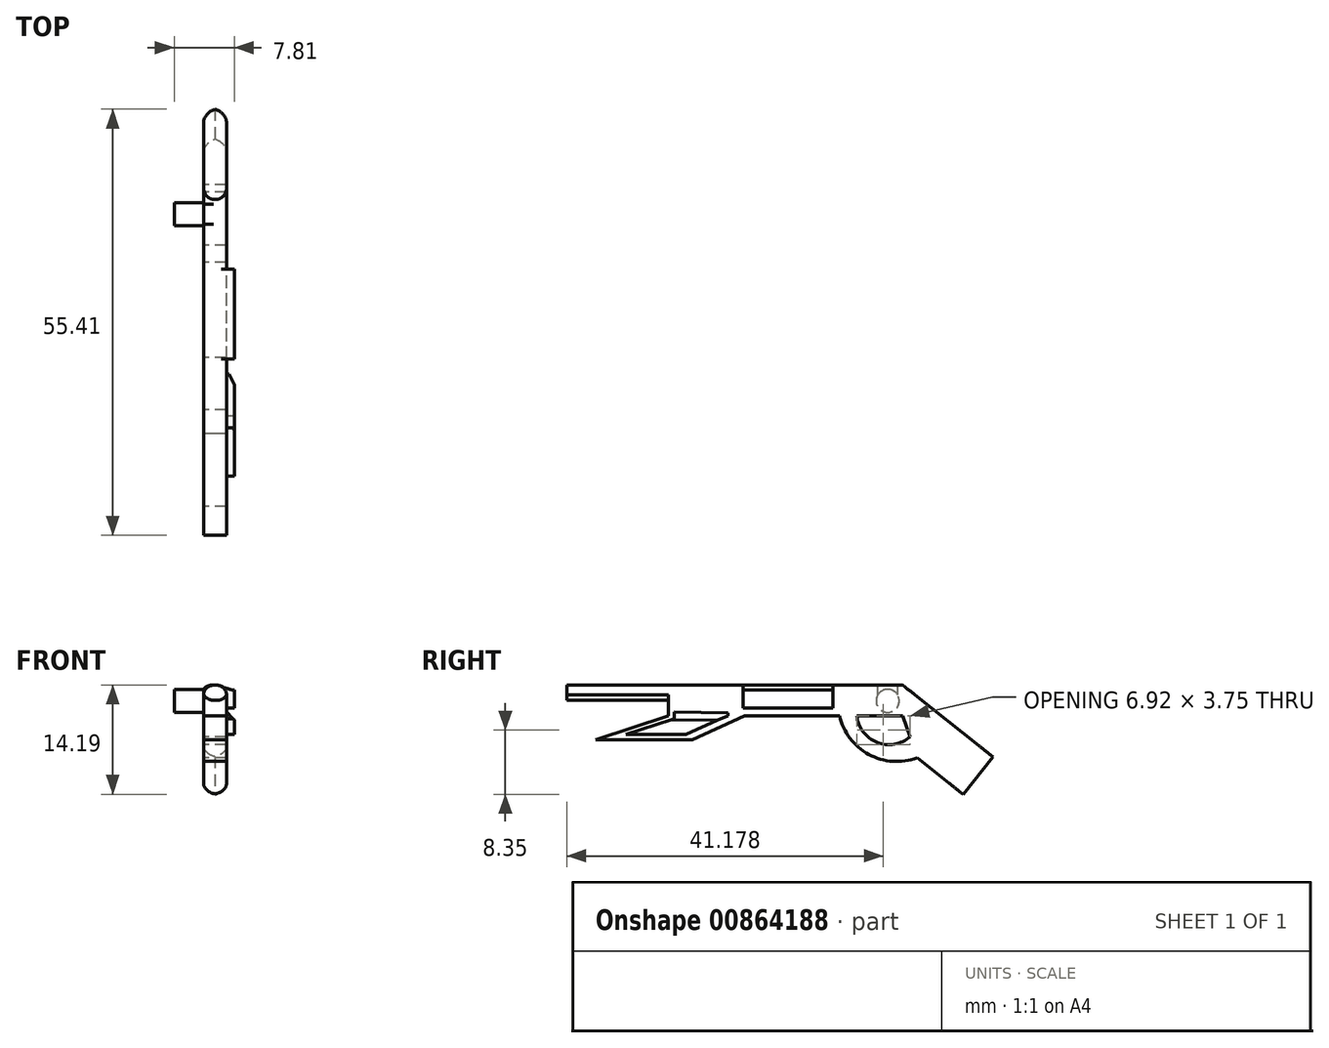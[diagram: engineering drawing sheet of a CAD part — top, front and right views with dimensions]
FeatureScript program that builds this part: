
annotation { "Feature Type Name" : "Feature", "Feature Type Description" : "" }
export const myFeature = defineFeature(function(context is Context, id is Id, definition is map)
    precondition{}
    {
        {
            var Q0;
            Q0=qCreatedBy(makeId("Right.planeOp"),FACE);
            var sketch = newSketch(context, id + "F0", { "sketchPlane" : qUnion([Q0])});
            skLineSegment(sketch, "E0.bottom", {"start": v(-13.26, 14.33) * mm, "end": v(17.22, 14.33) * mm});
            skLineSegment(sketch, "E0.top", {"start": v(-13.26, 10.36) * mm, "end": v(17.22, 10.36) * mm});
            skLineSegment(sketch, "E0.left", {"start": v(-13.26, 14.33) * mm, "end": v(-13.26, 10.36) * mm});
            skLineSegment(sketch, "E0.right", {"start": v(17.22, 14.33) * mm, "end": v(17.22, 10.36) * mm});
            skLineSegment(sketch, "E1", {"start": v(17.22, 14.33) * mm, "end": v(29.1, 4.88) * mm});
            skLineSegment(sketch, "E2", {"start": v(29.1, 4.88) * mm, "end": v(25.23, 0) * mm});
            skLineSegment(sketch, "E3", {"start": v(25.23, 0) * mm, "end": v(19.1, 4.88) * mm});
            skLineSegment(sketch, "E4", {"start": v(19.1, 4.88) * mm, "end": v(17.22, 10.36) * mm});
            skArc(sketch, "E5", {"start": v(9, 10.36) * mm, "mid": v(12.8, 5.32) * mm, "end": v(19.1, 4.88) * mm});
            skArc(sketch, "E6", {"start": v(11.24, 10.36) * mm, "mid": v(13.86, 6.89) * mm, "end": v(18.16, 7.62) * mm});
            skLineSegment(sketch, "E7", {"start": v(-3.39, 10.36) * mm, "end": v(-10.19, 7.24) * mm});
            skLineSegment(sketch, "E8", {"start": v(-10.19, 7.24) * mm, "end": v(-22.76, 7.24) * mm});
            skLineSegment(sketch, "E9", {"start": v(-22.76, 7.24) * mm, "end": v(-13.26, 10.36) * mm});
            skLineSegment(sketch, "E10", {"start": v(-13.26, 12.34) * mm, "end": v(-26.48, 12.34) * mm});
            skLineSegment(sketch, "E11", {"start": v(-26.48, 12.34) * mm, "end": v(-26.48, 14.33) * mm});
            skLineSegment(sketch, "E12", {"start": v(-26.48, 14.33) * mm, "end": v(-13.26, 14.33) * mm});
            skSolve(sketch);
        }
        {
            var Q0;
            {var subQ2=sQuery(id+"F0.wireOp",EDGE,"E10");Q0=makeQuery(id+"F0.imprint","IMPRINT",FACE,{"disambiguationData":[TD([[makeQuery(id+"F0.imprint","IMPRINT",EDGE,{"derivedFrom":subQ2}),-1.0]])]});}
            var Q1;
            {var subQ2=sQuery(id+"F0.wireOp",EDGE,"E7");Q1=makeQuery(id+"F0.imprint","IMPRINT",FACE,{"disambiguationData":[TD([[makeQuery(id+"F0.imprint","IMPRINT",EDGE,{"derivedFrom":subQ2}),-1.0]])]});}
            var Q2;
            {var subQ6=sQuery(id+"F0.wireOp",EDGE,"E0.bottom");Q2=makeQuery(id+"F0.imprint","IMPRINT",FACE,{"disambiguationData":[TD([[makeQuery(id+"F0.imprint","IMPRINT",EDGE,{"derivedFrom":subQ6}),-1.0]])]});}
            var Q3;
            {var subQ0=sQuery(id+"F0.wireOp",EDGE,"E5");Q3=makeQuery(id+"F0.imprint","IMPRINT",FACE,{"disambiguationData":[TD([[makeQuery(id+"F0.imprint","IMPRINT",EDGE,{"derivedFrom":subQ0}),1.0]])]});}
            var Q4;
            {var subQ1=sQuery(id+"F0.wireOp",EDGE,"E0.right");Q4=makeQuery(id+"F0.imprint","IMPRINT",FACE,{"disambiguationData":[TD([[makeQuery(id+"F0.imprint","IMPRINT",EDGE,{"derivedFrom":subQ1}),1.0]])]});}
            extrude(context, id + "F1", {"entities" : qUnion([Q0, Q1, Q2, Q3, Q4]), "depth" : 3 * mm, "offsetDistance" : 25.4 * mm});
        }
        {
            var Q0;
            Q0=makeQuery(id+"F1.opExtrude","CAP_FACE",FACE,{"disambiguationData":[OSD([sQuery(id+"F0.wireOp",EDGE,"E0.bottom"),sQuery(id+"F0.wireOp",EDGE,"E0.top"),sQuery(id+"F0.wireOp",EDGE,"E0.left"),sQuery(id+"F0.wireOp",EDGE,"E1"),sQuery(id+"F0.wireOp",EDGE,"E2"),sQuery(id+"F0.wireOp",EDGE,"E3"),sQuery(id+"F0.wireOp",EDGE,"E4"),sQuery(id+"F0.wireOp",EDGE,"E5"),sQuery(id+"F0.wireOp",EDGE,"E6"),sQuery(id+"F0.wireOp",EDGE,"E7"),sQuery(id+"F0.wireOp",EDGE,"E8"),sQuery(id+"F0.wireOp",EDGE,"E9"),sQuery(id+"F0.wireOp",EDGE,"E10"),sQuery(id+"F0.wireOp",EDGE,"E11"),sQuery(id+"F0.wireOp",EDGE,"E12")])],"isStart":false});
            var sketch = newSketch(context, id + "F2", { "sketchPlane" : qUnion([Q0])});
            skLineSegment(sketch, "E13", {"start": v(-12.48, 12.39) * mm, "end": v(-12.48, 9.99) * mm});
            skLineSegment(sketch, "E14", {"start": v(-12.48, 9.99) * mm, "end": v(-18.8, 7.9) * mm});
            skLineSegment(sketch, "E15", {"start": v(-18.8, 7.9) * mm, "end": v(-10.97, 7.9) * mm});
            skLineSegment(sketch, "E16", {"start": v(-10.97, 7.9) * mm, "end": v(-5.54, 10.36) * mm});
            skLineSegment(sketch, "E17", {"start": v(-5.54, 10.36) * mm, "end": v(-5.54, 12.25) * mm});
            skLineSegment(sketch, "E18", {"start": v(-5.54, 12.25) * mm, "end": v(-12.48, 12.39) * mm});
            skLineSegment(sketch, "E19.bottom", {"start": v(-3.54, 13.68) * mm, "end": v(8.16, 13.68) * mm});
            skLineSegment(sketch, "E19.top", {"start": v(-3.54, 11.32) * mm, "end": v(8.16, 11.32) * mm});
            skLineSegment(sketch, "E19.left", {"start": v(-3.54, 13.68) * mm, "end": v(-3.54, 11.32) * mm});
            skLineSegment(sketch, "E19.right", {"start": v(8.16, 13.68) * mm, "end": v(8.16, 11.32) * mm});
            skSolve(sketch);
        }
        {
            var Q0;
            Q0=makeQuery(id+"F2.imprint","IMPRINT",FACE,{"disambiguationData":[TD([[makeQuery(id+"F2.imprint","IMPRINT",EDGE,{"derivedFrom":sQuery(id+"F2.wireOp",EDGE,"E13")}),1.0]])]});
            var Q1;
            Q1=makeQuery(id+"F2.imprint","IMPRINT",FACE,{"disambiguationData":[TD([[makeQuery(id+"F2.imprint","IMPRINT",EDGE,{"derivedFrom":sQuery(id+"F2.wireOp",EDGE,"E19.bottom")}),-1.0]])]});
            extrude(context, id + "F3", {"entities" : qUnion([Q0, Q1]), "operationType" : NewBodyOperationType.ADD, "depth" : 1 * mm, "offsetDistance" : 25.4 * mm});
        }
        {
            var Q0;
            Q0=makeQuery(id+"F1.opExtrude","CAP_FACE",FACE,{"disambiguationData":[OSD([sQuery(id+"F0.wireOp",EDGE,"E0.bottom"),sQuery(id+"F0.wireOp",EDGE,"E0.top"),sQuery(id+"F0.wireOp",EDGE,"E0.left"),sQuery(id+"F0.wireOp",EDGE,"E1"),sQuery(id+"F0.wireOp",EDGE,"E2"),sQuery(id+"F0.wireOp",EDGE,"E3"),sQuery(id+"F0.wireOp",EDGE,"E4"),sQuery(id+"F0.wireOp",EDGE,"E5"),sQuery(id+"F0.wireOp",EDGE,"E6"),sQuery(id+"F0.wireOp",EDGE,"E7"),sQuery(id+"F0.wireOp",EDGE,"E8"),sQuery(id+"F0.wireOp",EDGE,"E9"),sQuery(id+"F0.wireOp",EDGE,"E10"),sQuery(id+"F0.wireOp",EDGE,"E11"),sQuery(id+"F0.wireOp",EDGE,"E12")])],"isStart":true});
            var sketch = newSketch(context, id + "F4", { "sketchPlane" : qUnion([Q0])});
            skCircle(sketch, "E20", {"center": v(-15.26, 12.28) * mm, "radius": 1.5 * mm});
            skSolve(sketch);
        }
        {
            var Q0;
            Q0=makeQuery(id+"F4.imprint","IMPRINT",FACE,{"disambiguationData":[TD([[makeQuery(id+"F4.imprint","IMPRINT",EDGE,{"derivedFrom":sQuery(id+"F4.wireOp",EDGE,"E20")}),1.0]])]});
            extrude(context, id + "F5", {"entities" : qUnion([Q0]), "operationType" : NewBodyOperationType.ADD, "depth" : 3.8 * mm, "offsetDistance" : 25.4 * mm});
        }
        {
            var Q0;
            Q0=makeQuery(id+"F1.opExtrude","CAP_EDGE",EDGE,{"disambiguationData":[OSD([sQuery(id+"F0.wireOp",EDGE,"E0.bottom"),sQuery(id+"F0.wireOp",EDGE,"E12")])],"isStart":false});
            var Q1;
            Q1=makeQuery(id+"F1.opExtrude","CAP_EDGE",EDGE,{"disambiguationData":[OSD([sQuery(id+"F0.wireOp",EDGE,"E0.bottom"),sQuery(id+"F0.wireOp",EDGE,"E12")])],"isStart":true});
            fillet(context, id + "F6", {"entities" : qUnion([Q0, Q1]), "radius" : 1.27 * mm, "tangentPropagation" : true, "allowEdgeOverflow" : false});
        }
        {
            var Q0;
            Q0=makeQuery(id+"F6.opFillet","BLEND_EDGE",EDGE,{"blendedFrom":[makeQuery(id+"F1.opExtrude","CAP_EDGE",EDGE,{"disambiguationData":[OSD([sQuery(id+"F0.wireOp",EDGE,"E0.bottom"),sQuery(id+"F0.wireOp",EDGE,"E12")])],"isStart":false}),makeQuery(id+"F3.opExtrude","SWEPT_FACE",FACE,{"disambiguationData":[OSD([sQuery(id+"F2.wireOp",EDGE,"E19.bottom")])]})],"blendedInto":[makeQuery(id+"F3.opExtrude","SWEPT_FACE",FACE,{"disambiguationData":[OSD([sQuery(id+"F2.wireOp",EDGE,"E19.bottom")])]})]});
            fillet(context, id + "F7", {"entities" : qUnion([Q0]), "radius" : 5.08 * mm, "tangentPropagation" : true, "allowEdgeOverflow" : false});
        }
        {
            var Q0;
            Q0=makeQuery(id+"F3.opExtrude","CAP_EDGE",EDGE,{"disambiguationData":[OSD([sQuery(id+"F2.wireOp",EDGE,"E18")])],"isStart":false});
            chamfer(context, id + "F8", {"entities" : qUnion([Q0]), "width" : 2.54 * mm, "tangentPropagation" : true});
        }
        {
            var Q0;
            Q0=makeQuery(id+"F1.opExtrude","CAP_EDGE",EDGE,{"disambiguationData":[OSD([sQuery(id+"F0.wireOp",EDGE,"E10")])],"isStart":false});
            fillet(context, id + "F9", {"entities" : qUnion([Q0]), "radius" : 1.52 * mm, "tangentPropagation" : true, "allowEdgeOverflow" : false});
        }
        {
            var Q0;
            Q0=makeQuery(id+"F1.opExtrude","CAP_EDGE",EDGE,{"disambiguationData":[OSD([sQuery(id+"F0.wireOp",EDGE,"E10")])],"isStart":true});
            fillet(context, id + "F10", {"entities" : qUnion([Q0]), "radius" : 1.78 * mm, "tangentPropagation" : true, "allowEdgeOverflow" : false});
        }
        {
            var Q0;
            Q0=makeQuery(id+"F1.opExtrude","CAP_EDGE",EDGE,{"disambiguationData":[OSD([sQuery(id+"F0.wireOp",EDGE,"E2")])],"isStart":false});
            var Q1;
            Q1=makeQuery(id+"F1.opExtrude","CAP_EDGE",EDGE,{"disambiguationData":[OSD([sQuery(id+"F0.wireOp",EDGE,"E2")])],"isStart":true});
            fillet(context, id + "F11", {"entities" : qUnion([Q0, Q1]), "radius" : 2.54 * mm, "tangentPropagation" : true, "allowEdgeOverflow" : false});
        }
    });
